# Revit family: TYCO-FPP-FireClass-FC410RIM RELAY IF MODULE
name_source: partatom
category: Electrical Fixtures
revit_build: Autodesk Revit 2014 (Build: 20130308_1515(x64)
units: mm (PartAtom-declared; Revit-internal decimal feet)

## types (1)
- TYCO-FPP-FireClass-FC410RIM RELAY IF MODULE
    Alarm Current mA = 4.6
    Description = Relay Interface Module
    Front cover = Yes
    Keynote = The relay state (activated, deactivated or stuck) is returned to the
controller as confirmation.
    Length = 61 mm
    Manufacturer = Tyco
    Model = FireClass- 568.800.703
    Operating Humidity = 10% to 95% non condensing
    Operating Temperature = –25°C to +70°C
    PCB = PCB
    Quiescent Current mA = 0.46
    Rear cover = Yes
    Storage Temperature = –40°C to +80°C
    Type Comments = The FC410RIM Relay Interface Module provides one volt-free relay
changeover contact on a latching relay.
    URL = https://fireclass.co.uk
    Width = 84 mm

## geometry (parser evidence)
native form markers: Sweep x3
no freeform markers — native parametric forms only
